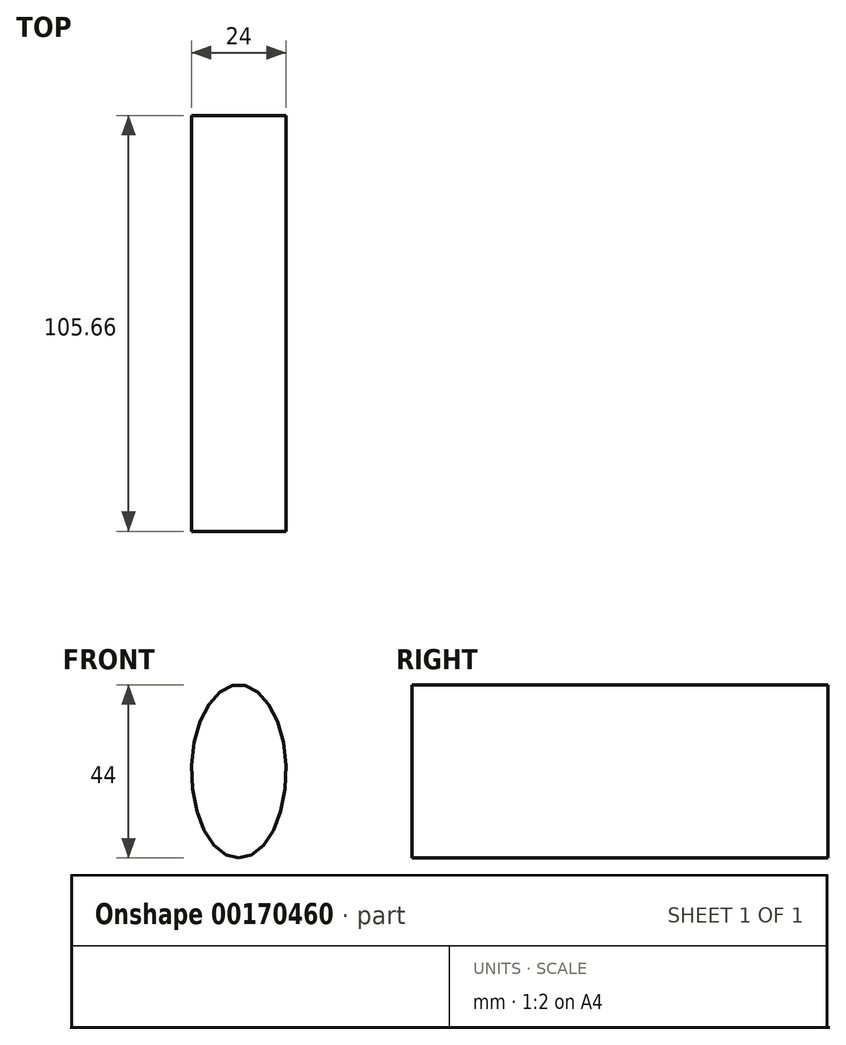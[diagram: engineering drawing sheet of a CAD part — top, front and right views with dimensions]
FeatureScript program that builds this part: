
annotation { "Feature Type Name" : "Feature", "Feature Type Description" : "" }
export const myFeature = defineFeature(function(context is Context, id is Id, definition is map)
    precondition{}
    {
        {
            var Q0;
            Q0=qCreatedBy(makeId("Front.planeOp"),FACE);
            var sketch = newSketch(context, id + "F0", { "sketchPlane" : qUnion([Q0])});
            skEllipse(sketch, "E0", {"center": v(0, 0) * mm, "majorRadius": 22 * mm, "minorRadius": 12 * mm, "majorAxis": v(0, -1)});
            skSolve(sketch);
        }
        {
            var Q0;
            Q0=makeQuery(id+"F0.imprint","IMPRINT",FACE,{"disambiguationData":[TD([[makeQuery(id+"F0.imprint","IMPRINT",EDGE,{"derivedFrom":sQuery(id+"F0.wireOp",EDGE,"E0")}),1.0]])]});
            extrude(context, id + "F1", {"entities" : qUnion([Q0]), "depth" : 80.26 * mm, "symmetric" : true});
        }
        {
            var Q0;
            Q0=qCreatedBy(makeId("Front.planeOp"),FACE);
            var sketch = newSketch(context, id + "F2", { "sketchPlane" : qUnion([Q0])});
            skLineSegment(sketch, "E1", {"start": v(0, 31.6) * mm, "end": v(0, -36.12) * mm});
            skSolve(sketch);
        }
        {
            var Q0;
            Q0=sQuery(id+"F2.wireOp",EDGE,"E1");
            var Q1;
            Q1=makeQuery(id+"F1.opExtrude","CAP_FACE",FACE,{"disambiguationData":[OSD([sQuery(id+"F0.wireOp",EDGE,"E0")])],"isStart":false});
            var Q2;
            Q2=makeQuery(id+"F1.opExtrude","CAP_FACE",FACE,{"disambiguationData":[OSD([sQuery(id+"F0.wireOp",EDGE,"E0")])],"isStart":true});
            extrude(context, id + "F3", {"bodyType" : ToolBodyType.SURFACE, "surfaceEntities" : qUnion([Q0]), "endBound" : BoundingType.UP_TO_SURFACE, "endBoundEntityFace" : qUnion([Q1]), "depth" : 77.72 * mm, "hasSecondDirection" : true, "secondDirectionBound" : BoundingType.UP_TO_SURFACE, "secondDirectionOppositeDirection" : true, "secondDirectionBoundEntityFace" : qUnion([Q2]), "secondDirectionDepth" : 25.4 * mm});
        }
        {
            var Q0;
            Q0=makeQuery(id+"F1.opExtrude","CAP_FACE",FACE,{"disambiguationData":[OSD([sQuery(id+"F0.wireOp",EDGE,"E0")])],"isStart":false});
            extrude(context, id + "F4", {"entities" : qUnion([Q0]), "operationType" : NewBodyOperationType.ADD, "depth" : 25.4 * mm, "offsetDistance" : 25.4 * mm});
        }
    });
